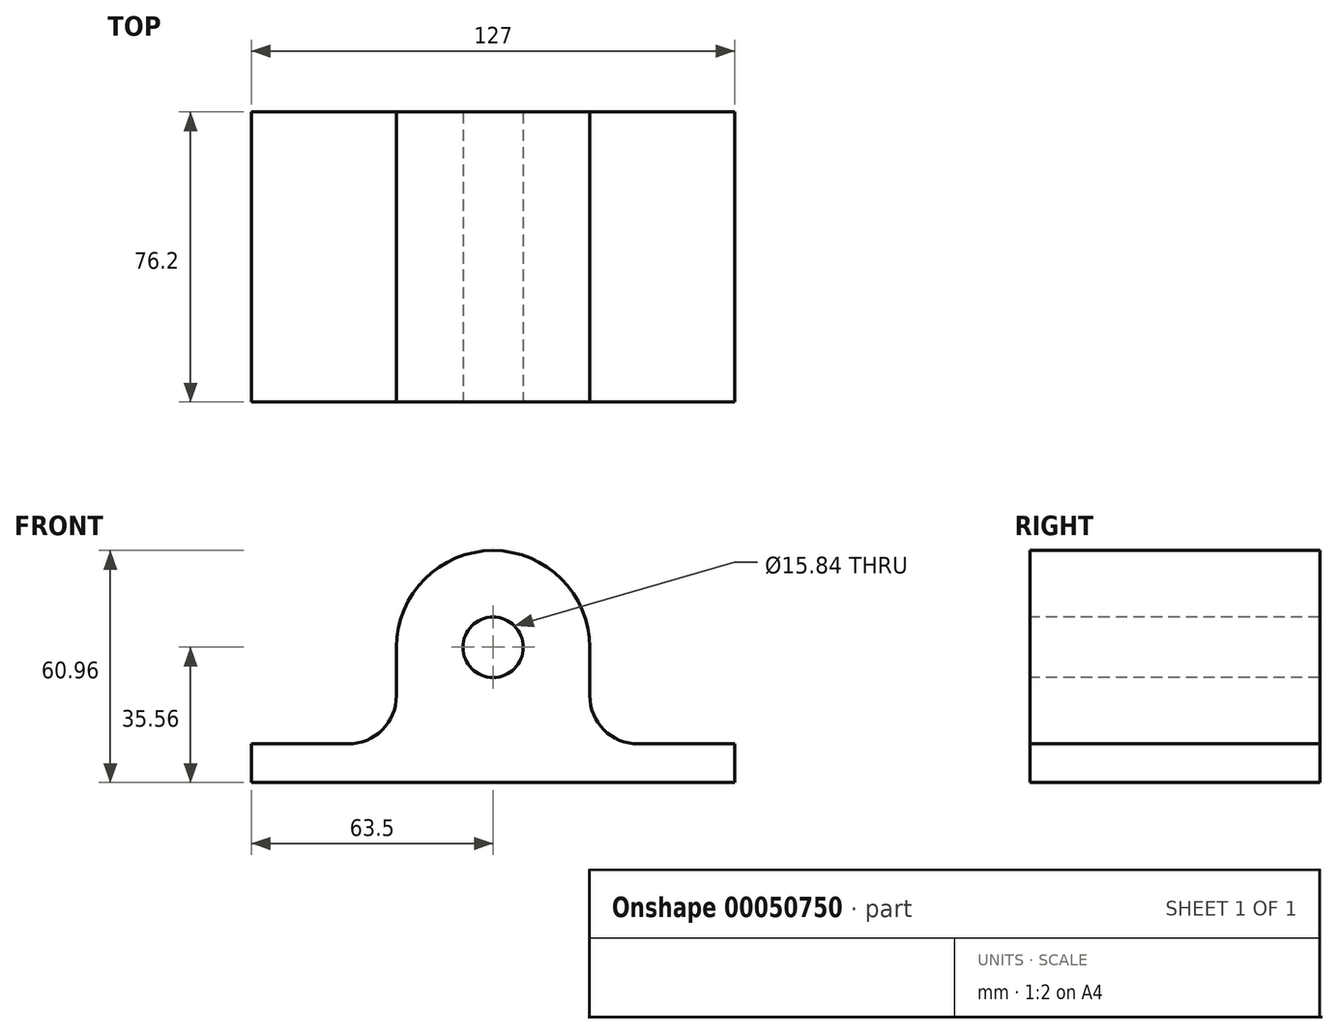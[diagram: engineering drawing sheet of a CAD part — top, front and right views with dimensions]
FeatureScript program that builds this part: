
annotation { "Feature Type Name" : "Feature", "Feature Type Description" : "" }
export const myFeature = defineFeature(function(context is Context, id is Id, definition is map)
    precondition{}
    {
        {
            var Q0;
            Q0=qCreatedBy(makeId("Front.planeOp"),FACE);
            var sketch = newSketch(context, id + "F0", { "sketchPlane" : qUnion([Q0])});
            skArc(sketch, "E0", {"start": v(25.4, 0) * mm, "mid": v(0, 25.4) * mm, "end": v(-25.4, 0) * mm});
            skLineSegment(sketch, "E1", {"start": v(63.5, -25.4) * mm, "end": v(63.5, -35.56) * mm});
            skLineSegment(sketch, "E2", {"start": v(63.5, -35.56) * mm, "end": v(-63.5, -35.56) * mm});
            skLineSegment(sketch, "E3", {"start": v(63.5, -25.4) * mm, "end": v(25.4, -25.4) * mm});
            skLineSegment(sketch, "E4", {"start": v(-63.5, -25.4) * mm, "end": v(-63.5, -35.56) * mm});
            skPoint(sketch, "E5.orphan", {"position": v(0, -25.4) * mm});
            skLineSegment(sketch, "E6", {"start": v(-25.4, 0) * mm, "end": v(-25.4, -25.4) * mm});
            skLineSegment(sketch, "E7", {"start": v(25.4, 0) * mm, "end": v(25.4, -25.4) * mm});
            skLineSegment(sketch, "E8.trimOffspring", {"start": v(-25.4, -25.4) * mm, "end": v(-63.5, -25.4) * mm});
            skSolve(sketch);
        }
        {
            var Q0;
            Q0=makeQuery(id+"F0.imprint","IMPRINT",FACE,{"disambiguationData":[TD([[makeQuery(id+"F0.imprint","IMPRINT",EDGE,{"derivedFrom":sQuery(id+"F0.wireOp",EDGE,"e93993bc-110a-4236-887e-3042d54ea965")}),-1.0]])]});
            var Q1;
            Q1=makeQuery(id+"F0.imprint","IMPRINT",FACE,{"disambiguationData":[TD([[makeQuery(id+"F0.imprint","IMPRINT",EDGE,{"derivedFrom":sQuery(id+"F0.wireOp",EDGE,"E0")}),1.0]])]});
            extrude(context, id + "F1", {"entities" : qUnion([Q0, Q1]), "depth" : 76.2 * mm});
        }
        {
            var Q0;
            Q0=makeQuery(id+"F1.opExtrude","SWEPT_EDGE",EDGE,{"disambiguationData":[OSD([sQuery(id+"F0.wireOp",EDGE,"E3"),sQuery(id+"F0.wireOp",EDGE,"E7")])]});
            var Q1;
            Q1=makeQuery(id+"F1.opExtrude","SWEPT_EDGE",EDGE,{"disambiguationData":[OSD([sQuery(id+"F0.wireOp",EDGE,"E6"),sQuery(id+"F0.wireOp",EDGE,"E8.trimOffspring")])]});
            fillet(context, id + "F2", {"entities" : qUnion([Q0, Q1]), "radius" : 12.7 * mm, "tangentPropagation" : true, "allowEdgeOverflow" : false});
        }
        {
            var Q0;
            Q0=makeQuery(id+"F1.opExtrude","CAP_FACE",FACE,{"disambiguationData":[OSD([sQuery(id+"F0.wireOp",EDGE,"E0"),sQuery(id+"F0.wireOp",EDGE,"E1"),sQuery(id+"F0.wireOp",EDGE,"E2"),sQuery(id+"F0.wireOp",EDGE,"E3"),sQuery(id+"F0.wireOp",EDGE,"E4"),sQuery(id+"F0.wireOp",EDGE,"E6"),sQuery(id+"F0.wireOp",EDGE,"E7"),sQuery(id+"F0.wireOp",EDGE,"E8.trimOffspring")])],"isStart":false});
            var sketch = newSketch(context, id + "F3", { "sketchPlane" : qUnion([Q0])});
            skCircle(sketch, "E9", {"center": v(0, 0) * mm, "radius": 7.92 * mm});
            skSolve(sketch);
        }
        {
            var Q0;
            Q0=makeQuery(id+"F3.imprint","IMPRINT",FACE,{"disambiguationData":[TD([[makeQuery(id+"F3.imprint","IMPRINT",EDGE,{"derivedFrom":sQuery(id+"F3.wireOp",EDGE,"E9")}),1.0]])]});
            extrude(context, id + "F4", {"entities" : qUnion([Q0]), "operationType" : NewBodyOperationType.REMOVE, "oppositeDirection" : true, "depth" : 101.6 * mm});
        }
    });
